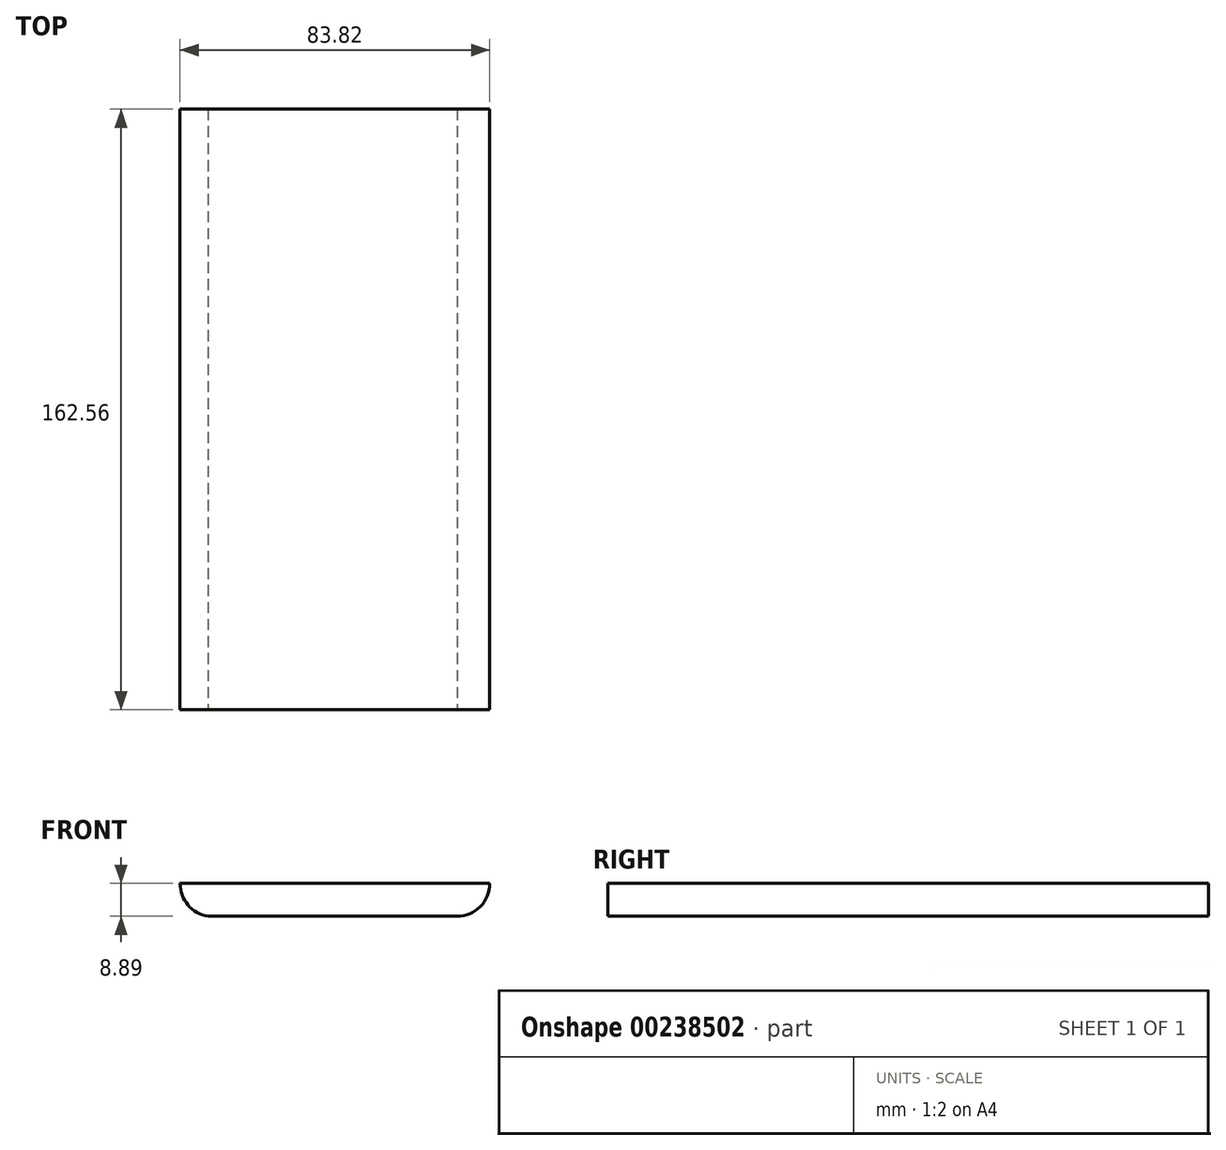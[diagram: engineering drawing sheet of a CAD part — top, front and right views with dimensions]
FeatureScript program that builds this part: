
annotation { "Feature Type Name" : "Feature", "Feature Type Description" : "" }
export const myFeature = defineFeature(function(context is Context, id is Id, definition is map)
    precondition{}
    {
        {
            var Q0;
            Q0=qCreatedBy(makeId("Right.planeOp"),FACE);
            var sketch = newSketch(context, id + "F0", { "sketchPlane" : qUnion([Q0])});
            skLineSegment(sketch, "E0.bottom", {"start": v(-80.64, 0) * mm, "end": v(81.92, 0) * mm});
            skLineSegment(sketch, "E0.top", {"start": v(-80.64, 8.9) * mm, "end": v(81.92, 8.9) * mm});
            skLineSegment(sketch, "E0.left", {"start": v(-80.64, 0) * mm, "end": v(-80.64, 8.9) * mm});
            skLineSegment(sketch, "E0.right", {"start": v(81.92, 0) * mm, "end": v(81.92, 8.9) * mm});
            skSolve(sketch);
        }
        {
            var Q0;
            Q0 = qSketchRegion(id + "F0", true);
            extrude(context, id + "F1", {"entities" : qUnion([Q0]), "depth" : 83.82 * mm});
        }
        {
            var Q0;
            Q0=makeQuery(id+"F1.opExtrude","SWEPT_FACE",FACE,{"disambiguationData":[OSD([sQuery(id+"F0.wireOp",EDGE,"E0.left")])]});
            var sketch = newSketch(context, id + "F2", { "sketchPlane" : qUnion([Q0])});
            skLineSegment(sketch, "E1", {"start": v(83.82, 0) * mm, "end": v(83.82, 8.9) * mm});
            skLineSegment(sketch, "E2", {"start": v(41.91, 8.9) * mm, "end": v(0, 8.9) * mm});
            skArc(sketch, "E3", {"start": v(0, 8.9) * mm, "mid": v(3.18, 2.02) * mm, "end": v(10.48, 0) * mm});
            skLineSegment(sketch, "E4", {"start": v(0, 8.9) * mm, "end": v(0, 0) * mm});
            skLineSegment(sketch, "E5", {"start": v(0, 0) * mm, "end": v(10.48, 0) * mm});
            skLineSegment(sketch, "E6", {"start": v(0, 0) * mm, "end": v(0, 8.9) * mm});
            skLineSegment(sketch, "E7", {"start": v(83.82, 8.9) * mm, "end": v(83.82, 8.9) * mm});
            skLineSegment(sketch, "E8", {"start": v(83.82, 0) * mm, "end": v(74.8, 0) * mm});
            skArc(sketch, "E9", {"start": v(74.8, 0) * mm, "mid": v(81.17, 2.56) * mm, "end": v(83.82, 8.9) * mm});
            skLineSegment(sketch, "E10", {"start": v(74.8, 0) * mm, "end": v(83.82, 0) * mm});
            skLineSegment(sketch, "E11", {"start": v(83.82, 8.9) * mm, "end": v(83.82, 0) * mm});
            skLineSegment(sketch, "E12", {"start": v(74.8, 0) * mm, "end": v(74.93, 8.9) * mm});
            skSolve(sketch);
        }
        {
            var Q0;
            Q0 = qSketchRegion(id + "F2", true);
            extrude(context, id + "F3", {"entities" : qUnion([Q0]), "operationType" : NewBodyOperationType.REMOVE, "oppositeDirection" : true, "depth" : 162.56 * mm});
        }
    });
